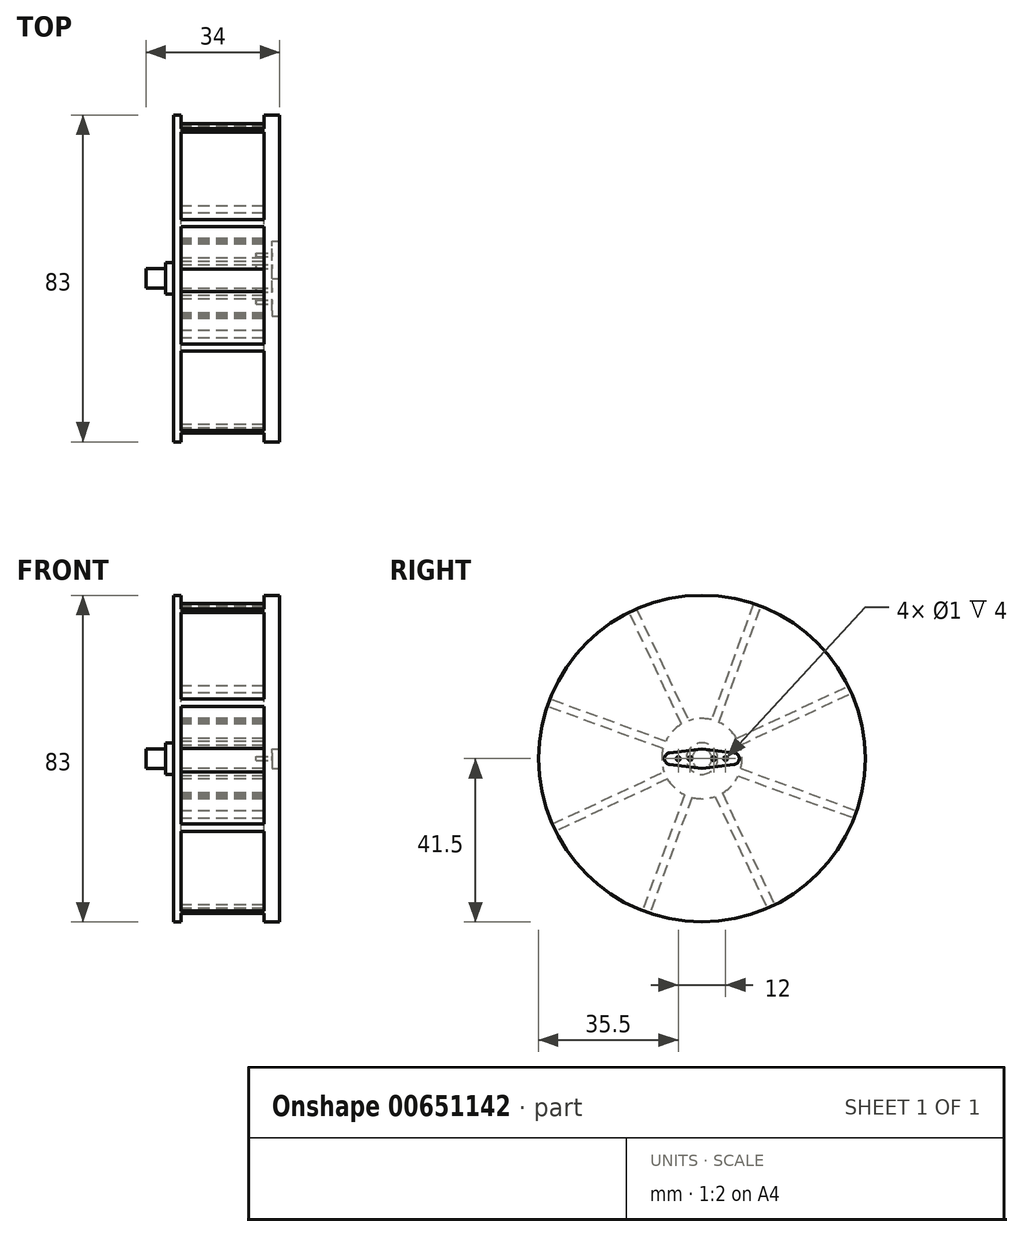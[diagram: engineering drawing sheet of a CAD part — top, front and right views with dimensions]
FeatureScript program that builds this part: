
annotation { "Feature Type Name" : "Feature", "Feature Type Description" : "" }
export const myFeature = defineFeature(function(context is Context, id is Id, definition is map)
    precondition{}
    {
        {
            var Q0;
            Q0=qCreatedBy(makeId("Right.planeOp"),FACE);
            var sketch = newSketch(context, id + "F0", { "sketchPlane" : qUnion([Q0])});
            skCircle(sketch, "E0", {"center": v(0, 0) * mm, "radius": 41.5 * mm});
            skSolve(sketch);
        }
        {
            var Q0;
            Q0=makeQuery(id+"F0.imprint","IMPRINT",FACE,{"disambiguationData":[TD([[makeQuery(id+"F0.imprint","IMPRINT",EDGE,{"derivedFrom":sQuery(id+"F0.wireOp",EDGE,"E0")}),1.0]])]});
            extrude(context, id + "F1", {"entities" : qUnion([Q0]), "depth" : 2 * mm, "offsetDistance" : 25 * mm});
        }
        {
            var Q0;
            Q0=makeQuery(id+"F1.opExtrude","CAP_FACE",FACE,{"disambiguationData":[OSD([sQuery(id+"F0.wireOp",EDGE,"E0")])],"isStart":false});
            var sketch = newSketch(context, id + "F2", { "sketchPlane" : qUnion([Q0])});
            skCircle(sketch, "E1", {"center": v(0, 0) * mm, "radius": 10.18 * mm});
            skLineSegment(sketch, "E2", {"start": v(4.28, 9.24) * mm, "end": v(15, 38.7) * mm});
            skLineSegment(sketch, "E3", {"start": v(13.12, 39.37) * mm, "end": v(2.4, 9.9) * mm});
            skArc(sketch, "E4", {"start": v(13.12, 39.37) * mm, "mid": v(14.07, 39.04) * mm, "end": v(15, 38.7) * mm});
            skLineSegment(sketch, "E5", {"start": v(8.76, 5.19) * mm, "end": v(37.18, 18.44) * mm});
            skLineSegment(sketch, "E6", {"start": v(9.6, 3.38) * mm, "end": v(38.02, 16.63) * mm});
            skLineSegment(sketch, "E7", {"start": v(9.86, -2.53) * mm, "end": v(39.33, -13.25) * mm});
            skLineSegment(sketch, "E8", {"start": v(9.18, -4.4) * mm, "end": v(38.64, -15.13) * mm});
            skLineSegment(sketch, "E9", {"start": v(5.19, -8.76) * mm, "end": v(18.44, -37.18) * mm});
            skLineSegment(sketch, "E10", {"start": v(3.38, -9.6) * mm, "end": v(16.63, -38.02) * mm});
            skLineSegment(sketch, "E11", {"start": v(-2.53, -9.86) * mm, "end": v(-13.25, -39.33) * mm});
            skLineSegment(sketch, "E12", {"start": v(-4.4, -9.18) * mm, "end": v(-15.13, -38.64) * mm});
            skLineSegment(sketch, "E13", {"start": v(-38.02, -16.63) * mm, "end": v(-9.6, -3.38) * mm});
            skLineSegment(sketch, "E14", {"start": v(-8.76, -5.19) * mm, "end": v(-37.18, -18.44) * mm});
            skLineSegment(sketch, "E15", {"start": v(-9.86, 2.53) * mm, "end": v(-39.33, 13.25) * mm});
            skLineSegment(sketch, "E16", {"start": v(-9.18, 4.4) * mm, "end": v(-38.64, 15.13) * mm});
            skLineSegment(sketch, "E17", {"start": v(-5.19, 8.76) * mm, "end": v(-18.44, 37.18) * mm});
            skLineSegment(sketch, "E18", {"start": v(-16.63, 38.02) * mm, "end": v(-3.38, 9.6) * mm});
            skSolve(sketch);
        }
        {
            var Q0;
            Q0 = qSketchRegion(id + "F2", true);
            var Q1;
            {var subQ0=sQuery(id+"F2.wireOp",EDGE,"E17");Q1=makeQuery(id+"F2.imprint","IMPRINT",FACE,{"disambiguationData":[TD([[makeQuery(id+"F2.imprint","IMPRINT",EDGE,{"derivedFrom":subQ0}),-1.0]])]});}
            var Q2;
            {var subQ0=sQuery(id+"F2.wireOp",EDGE,"E5");Q2=makeQuery(id+"F2.imprint","IMPRINT",FACE,{"disambiguationData":[TD([[makeQuery(id+"F2.imprint","IMPRINT",EDGE,{"derivedFrom":subQ0}),-1.0]])]});}
            var Q3;
            {var subQ0=sQuery(id+"F2.wireOp",EDGE,"E7");Q3=makeQuery(id+"F2.imprint","IMPRINT",FACE,{"disambiguationData":[TD([[makeQuery(id+"F2.imprint","IMPRINT",EDGE,{"derivedFrom":subQ0}),-1.0]])]});}
            var Q4;
            {var subQ0=sQuery(id+"F2.wireOp",EDGE,"E9");Q4=makeQuery(id+"F2.imprint","IMPRINT",FACE,{"disambiguationData":[TD([[makeQuery(id+"F2.imprint","IMPRINT",EDGE,{"derivedFrom":subQ0}),-1.0]])]});}
            var Q5;
            {var subQ0=sQuery(id+"F2.wireOp",EDGE,"E11");Q5=makeQuery(id+"F2.imprint","IMPRINT",FACE,{"disambiguationData":[TD([[makeQuery(id+"F2.imprint","IMPRINT",EDGE,{"derivedFrom":subQ0}),-1.0]])]});}
            var Q6;
            {var subQ0=sQuery(id+"F2.wireOp",EDGE,"E15");Q6=makeQuery(id+"F2.imprint","IMPRINT",FACE,{"disambiguationData":[TD([[makeQuery(id+"F2.imprint","IMPRINT",EDGE,{"derivedFrom":subQ0}),-1.0]])]});}
            var Q7;
            {var subQ0=sQuery(id+"F2.wireOp",EDGE,"E13");Q7=makeQuery(id+"F2.imprint","IMPRINT",FACE,{"disambiguationData":[TD([[makeQuery(id+"F2.imprint","IMPRINT",EDGE,{"derivedFrom":subQ0}),-1.0]])]});}
            extrude(context, id + "F3", {"entities" : qUnion([Q0, Q1, Q2, Q3, Q4, Q5, Q6, Q7]), "operationType" : NewBodyOperationType.ADD, "depth" : 21 * mm, "offsetDistance" : 25 * mm});
        }
        {
            var Q0;
            Q0=makeQuery(id+"F3.opExtrude","CAP_FACE",FACE,{"disambiguationData":[OSD([sQuery(id+"F0.wireOp",EDGE,"E0"),sQuery(id+"F2.wireOp",EDGE,"E1"),sQuery(id+"F2.wireOp",EDGE,"E2"),sQuery(id+"F2.wireOp",EDGE,"E3"),sQuery(id+"F2.wireOp",EDGE,"E4"),sQuery(id+"F2.wireOp",EDGE,"E5"),sQuery(id+"F2.wireOp",EDGE,"E6"),sQuery(id+"F2.wireOp",EDGE,"E7"),sQuery(id+"F2.wireOp",EDGE,"E8"),sQuery(id+"F2.wireOp",EDGE,"E9"),sQuery(id+"F2.wireOp",EDGE,"E10"),sQuery(id+"F2.wireOp",EDGE,"E11"),sQuery(id+"F2.wireOp",EDGE,"E12"),sQuery(id+"F2.wireOp",EDGE,"E13"),sQuery(id+"F2.wireOp",EDGE,"E14"),sQuery(id+"F2.wireOp",EDGE,"E15"),sQuery(id+"F2.wireOp",EDGE,"E16"),sQuery(id+"F2.wireOp",EDGE,"E17"),sQuery(id+"F2.wireOp",EDGE,"E18")])],"isStart":false});
            var sketch = newSketch(context, id + "F4", { "sketchPlane" : qUnion([Q0])});
            skCircle(sketch, "E19", {"center": v(0, 0) * mm, "radius": 41.5 * mm});
            skSolve(sketch);
        }
        {
            var Q0;
            Q0 = qSketchRegion(id + "F4", true);
            extrude(context, id + "F5", {"entities" : qUnion([Q0]), "operationType" : NewBodyOperationType.ADD, "depth" : 2 * mm, "offsetDistance" : 25 * mm});
        }
        {
            var Q0;
            Q0=makeQuery(id+"F1.opExtrude","CAP_FACE",FACE,{"disambiguationData":[OSD([sQuery(id+"F0.wireOp",EDGE,"E0")])],"isStart":true});
            var sketch = newSketch(context, id + "F6", { "sketchPlane" : qUnion([Q0])});
            skCircle(sketch, "E20", {"center": v(0, 0) * mm, "radius": 4 * mm});
            skCircle(sketch, "E21", {"center": v(0, 0) * mm, "radius": 2.5 * mm});
            skSolve(sketch);
        }
        {
            var Q0;
            Q0 = qSketchRegion(id + "F6", true);
            extrude(context, id + "F7", {"entities" : qUnion([Q0]), "operationType" : NewBodyOperationType.ADD, "depth" : 2 * mm, "offsetDistance" : 25 * mm});
        }
        {
            var Q0;
            Q0=makeQuery(id+"F7.boolean.opBoolean","SPLIT",FACE,{"disambiguationData":[TD([makeQuery(id+"F7.opExtrude","SWEPT_FACE",FACE,{"disambiguationData":[OSD([sQuery(id+"F6.wireOp",EDGE,"E21")])]})])],"derivedFrom":makeQuery(id+"F1.opExtrude","CAP_FACE",FACE,{"disambiguationData":[OSD([sQuery(id+"F0.wireOp",EDGE,"E0")])],"isStart":true})});
            extrude(context, id + "F8", {"entities" : qUnion([Q0]), "operationType" : NewBodyOperationType.ADD, "depth" : 7 * mm, "offsetDistance" : 25 * mm});
        }
        {
            var Q0;
            Q0=makeQuery(id+"F5.opExtrude","CAP_FACE",FACE,{"disambiguationData":[OSD([sQuery(id+"F4.wireOp",EDGE,"E19")])],"isStart":false});
            var sketch = newSketch(context, id + "F9", { "sketchPlane" : qUnion([Q0])});
            skCircle(sketch, "E22", {"center": v(0, 0) * mm, "radius": 41.5 * mm});
            skSolve(sketch);
        }
        {
            var Q0;
            Q0=makeQuery(id+"F9.imprint","IMPRINT",FACE,{"disambiguationData":[TD([[makeQuery(id+"F9.imprint","IMPRINT",EDGE,{"derivedFrom":sQuery(id+"F9.wireOp",EDGE,"E22")}),1.0]])]});
            var sketch = newSketch(context, id + "F10", { "sketchPlane" : qUnion([Q0])});
            skCircle(sketch, "E23", {"center": v(0, 0) * mm, "radius": 41.5 * mm});
            skSolve(sketch);
        }
        {
            var Q0;
            Q0=makeQuery(id+"F10.imprint","IMPRINT",FACE,{"disambiguationData":[TD([[makeQuery(id+"F10.imprint","IMPRINT",EDGE,{"derivedFrom":sQuery(id+"F10.wireOp",EDGE,"E23")}),1.0]])]});
            extrude(context, id + "F11", {"entities" : qUnion([Q0]), "operationType" : NewBodyOperationType.ADD, "depth" : 2 * mm, "offsetDistance" : 25 * mm});
        }
        {
            var Q0;
            Q0=qCreatedBy(makeId("Right.planeOp"),FACE);
            var sketch = newSketch(context, id + "F12", { "sketchPlane" : qUnion([Q0])});
            skArc(sketch, "E24", {"start": v(0.31, 2.48) * mm, "mid": v(0, 2.5) * mm, "end": v(-0.31, 2.48) * mm});
            skArc(sketch, "E25", {"start": v(-8.19, 1.49) * mm, "mid": v(-9.5, 0) * mm, "end": v(-8.19, -1.49) * mm});
            skArc(sketch, "E26", {"start": v(8.19, -1.49) * mm, "mid": v(9.5, 0) * mm, "end": v(8.19, 1.49) * mm});
            skLineSegment(sketch, "E27", {"start": v(-8.19, 1.49) * mm, "end": v(0, 2.52) * mm});
            skLineSegment(sketch, "E28", {"start": v(-8.19, -1.49) * mm, "end": v(0, -2.52) * mm});
            skLineSegment(sketch, "E29", {"start": v(0, -2.52) * mm, "end": v(8.19, -1.49) * mm});
            skLineSegment(sketch, "E30", {"start": v(0, 2.52) * mm, "end": v(8.19, 1.49) * mm});
            skCircle(sketch, "E31", {"center": v(-3, 0) * mm, "radius": 0.5 * mm});
            skCircle(sketch, "E32", {"center": v(-6, 0) * mm, "radius": 0.5 * mm});
            skCircle(sketch, "E33", {"center": v(3, 0) * mm, "radius": 0.5 * mm});
            skCircle(sketch, "E34", {"center": v(6, 0) * mm, "radius": 0.5 * mm});
            skArc(sketch, "E35.trimOffspring", {"start": v(-0.31, -2.48) * mm, "mid": v(0, -2.5) * mm, "end": v(0.31, -2.48) * mm});
            skSolve(sketch);
        }
        {
            var Q0;
            Q0=makeQuery(id+"F11.opExtrude","CAP_FACE",FACE,{"disambiguationData":[OSD([sQuery(id+"F10.wireOp",EDGE,"E23")])],"isStart":false});
            var sketch = newSketch(context, id + "F13", { "sketchPlane" : qUnion([Q0])});
            skArc(sketch, "E36.0", {"start": v(8.19, -1.49) * mm, "mid": v(9.5, 0) * mm, "end": v(8.19, 1.49) * mm});
            skPoint(sketch, "E37.1", {"position": v(0, -2.5) * mm});
            skArc(sketch, "E38.0", {"start": v(-8.19, 1.49) * mm, "mid": v(-9.5, 0) * mm, "end": v(-8.19, -1.49) * mm});
            skCircle(sketch, "E39.0", {"center": v(6, 0) * mm, "radius": 0.5 * mm});
            skCircle(sketch, "E39.1", {"center": v(3, 0) * mm, "radius": 0.5 * mm});
            skCircle(sketch, "E40.0", {"center": v(-3, 0) * mm, "radius": 0.5 * mm});
            skCircle(sketch, "E40.1", {"center": v(-6, 0) * mm, "radius": 0.5 * mm});
            skLineSegment(sketch, "E41", {"start": v(-8.19, 1.49) * mm, "end": v(0, 2.52) * mm});
            skLineSegment(sketch, "E42", {"start": v(-8.19, -1.49) * mm, "end": v(0, -2.5) * mm});
            skLineSegment(sketch, "E43", {"start": v(0, 2.52) * mm, "end": v(8.19, 1.49) * mm});
            skLineSegment(sketch, "E44", {"start": v(0, -2.5) * mm, "end": v(8.19, -1.49) * mm});
            skSolve(sketch);
        }
        {
            var Q0;
            Q0=makeQuery(id+"F13.imprint","IMPRINT",FACE,{"disambiguationData":[TD([[makeQuery(id+"F13.imprint","IMPRINT",EDGE,{"derivedFrom":sQuery(id+"F13.wireOp",EDGE,"E36.0")}),1.0]])]});
            extrude(context, id + "F14", {"entities" : qUnion([Q0]), "operationType" : NewBodyOperationType.REMOVE, "oppositeDirection" : true, "depth" : 2 * mm, "offsetDistance" : 25 * mm});
        }
        {
            var Q0;
            Q0=makeQuery(id+"F14.boolean.opBoolean","SPLIT",FACE,{"disambiguationData":[TD([makeQuery(id+"F14.opExtrude","SWEPT_FACE",FACE,{"disambiguationData":[OSD([sQuery(id+"F13.wireOp",EDGE,"E40.0")])]})])],"derivedFrom":makeQuery(id+"F11.opExtrude","CAP_FACE",FACE,{"disambiguationData":[OSD([sQuery(id+"F10.wireOp",EDGE,"E23")])],"isStart":false})});
            var Q1;
            Q1=makeQuery(id+"F14.boolean.opBoolean","SPLIT",FACE,{"disambiguationData":[TD([makeQuery(id+"F14.opExtrude","SWEPT_FACE",FACE,{"disambiguationData":[OSD([sQuery(id+"F13.wireOp",EDGE,"E40.1")])]})])],"derivedFrom":makeQuery(id+"F11.opExtrude","CAP_FACE",FACE,{"disambiguationData":[OSD([sQuery(id+"F10.wireOp",EDGE,"E23")])],"isStart":false})});
            var Q2;
            Q2=makeQuery(id+"F14.boolean.opBoolean","SPLIT",FACE,{"disambiguationData":[TD([makeQuery(id+"F14.opExtrude","SWEPT_FACE",FACE,{"disambiguationData":[OSD([sQuery(id+"F13.wireOp",EDGE,"E39.1")])]})])],"derivedFrom":makeQuery(id+"F11.opExtrude","CAP_FACE",FACE,{"disambiguationData":[OSD([sQuery(id+"F10.wireOp",EDGE,"E23")])],"isStart":false})});
            var Q3;
            Q3=makeQuery(id+"F14.boolean.opBoolean","SPLIT",FACE,{"disambiguationData":[TD([makeQuery(id+"F14.opExtrude","SWEPT_FACE",FACE,{"disambiguationData":[OSD([sQuery(id+"F13.wireOp",EDGE,"E39.0")])]})])],"derivedFrom":makeQuery(id+"F11.opExtrude","CAP_FACE",FACE,{"disambiguationData":[OSD([sQuery(id+"F10.wireOp",EDGE,"E23")])],"isStart":false})});
            extrude(context, id + "F15", {"entities" : qUnion([Q0, Q1, Q2, Q3]), "operationType" : NewBodyOperationType.REMOVE, "oppositeDirection" : true, "depth" : 6 * mm, "offsetDistance" : 25 * mm});
        }
    });
